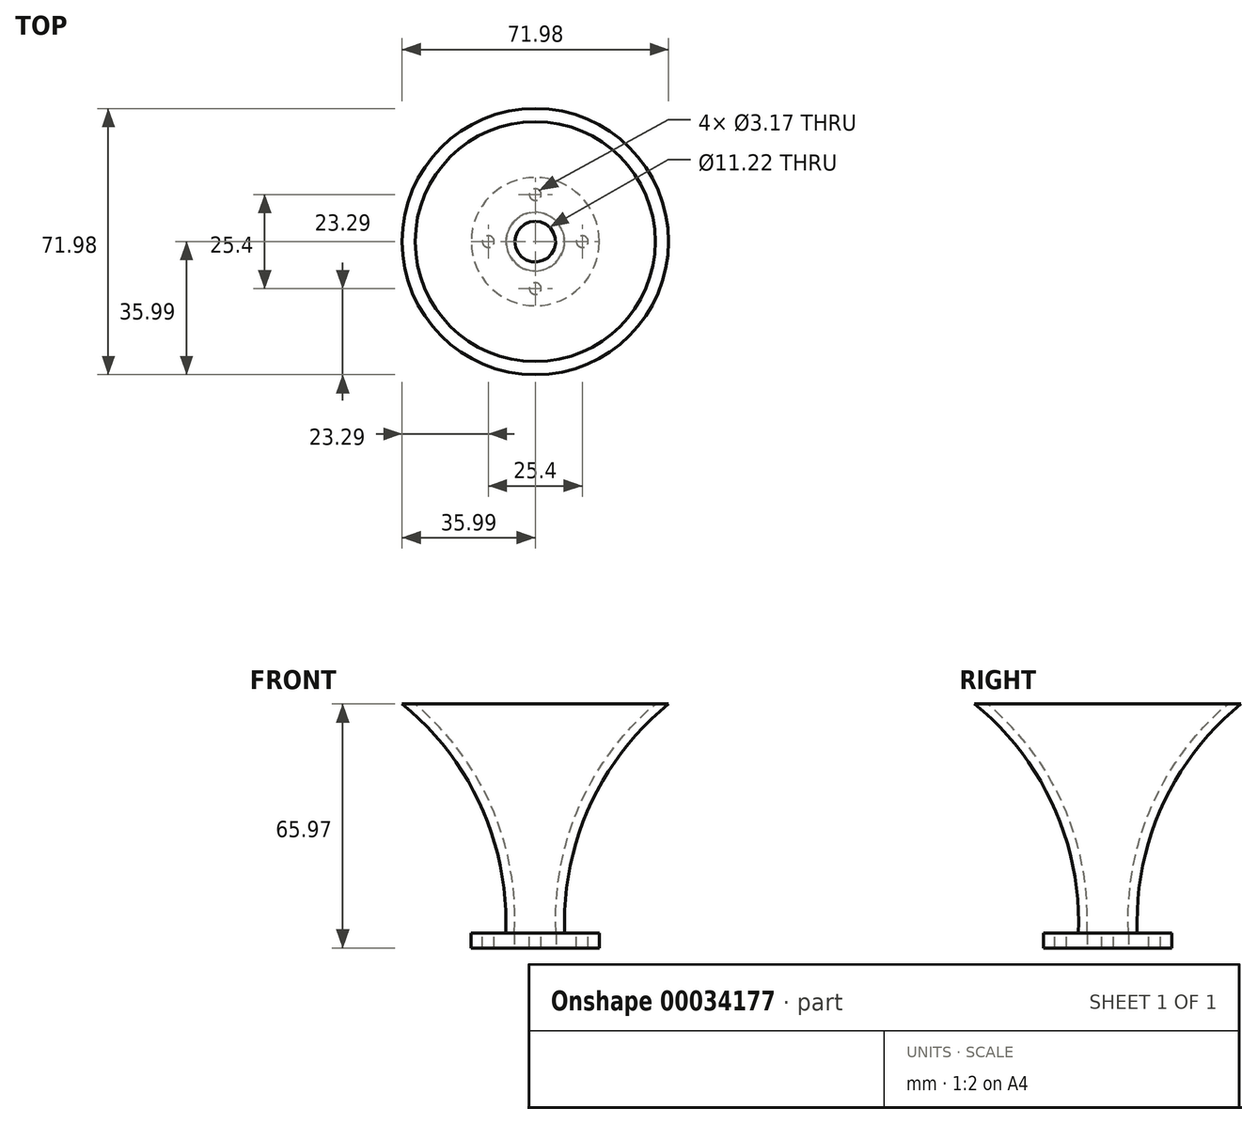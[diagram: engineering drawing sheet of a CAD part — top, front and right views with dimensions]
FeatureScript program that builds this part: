
annotation { "Feature Type Name" : "Feature", "Feature Type Description" : "" }
export const myFeature = defineFeature(function(context is Context, id is Id, definition is map)
    precondition{}
    {
        {
            var Q0;
            Q0=qCreatedBy(makeId("Front.planeOp"),FACE);
            var sketch = newSketch(context, id + "F0", { "sketchPlane" : qUnion([Q0])});
            skLineSegment(sketch, "E0", {"start": v(0, 0) * mm, "end": v(0, 61.95) * mm});
            skArc(sketch, "E1", {"start": v(35.99, 61.95) * mm, "mid": v(14.67, 34.28) * mm, "end": v(7.96, 0) * mm});
            skLineSegment(sketch, "E2", {"start": v(0, 76.37) * mm, "end": v(0, -15.4) * mm, "construction": true});
            skPoint(sketch, "E2.endSnap0", {"position": v(0, 30.98) * mm});
            skArc(sketch, "E3", {"start": v(32.43, 61.9) * mm, "mid": v(11.78, 34.08) * mm, "end": v(5.6, 0) * mm});
            skLineSegment(sketch, "E4", {"start": v(32.43, 61.9) * mm, "end": v(35.99, 61.95) * mm});
            skLineSegment(sketch, "E5", {"start": v(5.6, 0) * mm, "end": v(7.96, 0) * mm});
            skLineSegment(sketch, "E6.bottom", {"start": v(5.6, 0) * mm, "end": v(17.3, 0) * mm});
            skLineSegment(sketch, "E6.top", {"start": v(5.6, -4.02) * mm, "end": v(17.3, -4.02) * mm});
            skLineSegment(sketch, "E6.left", {"start": v(5.6, 0) * mm, "end": v(5.6, -4.02) * mm});
            skLineSegment(sketch, "E6.right", {"start": v(17.3, 0) * mm, "end": v(17.3, -4.02) * mm});
            skSolve(sketch);
        }
        {
            var Q0;
            Q0 = qSketchRegion(id + "F0", true);
            var Q1;
            Q1=sQuery(id+"F0.wireOp",EDGE,"E0");
            revolve(context, id + "F1", {"entities" : qUnion([Q0]), "axis" : qUnion([Q1]), "revolveType" : RevolveType.FULL});
        }
        {
            var Q0;
            Q0=qCreatedBy(makeId("Top.planeOp"),FACE);
            var sketch = newSketch(context, id + "F2", { "sketchPlane" : qUnion([Q0])});
            skCircle(sketch, "E7", {"center": v(0, 0) * mm, "radius": 12.7 * mm, "construction": true});
            skCircle(sketch, "E8", {"center": v(0, -12.7) * mm, "radius": 1.59 * mm});
            skCircle(sketch, "E9.1.0", {"center": v(12.7, 0) * mm, "radius": 1.59 * mm});
            skCircle(sketch, "E9.2.0", {"center": v(0, 12.7) * mm, "radius": 1.59 * mm});
            skCircle(sketch, "E9.3.0", {"center": v(-12.7, 0) * mm, "radius": 1.59 * mm});
            skSolve(sketch);
        }
        {
            var Q0;
            Q0=sQuery(id+"F2.wireOp",VERTEX,"E9.3.0.center");
            var Q1;
            Q1=sQuery(id+"F2.wireOp",VERTEX,"E8.center");
            var Q2;
            Q2=sQuery(id+"F2.wireOp",VERTEX,"E9.1.0.center");
            var Q3;
            Q3=sQuery(id+"F2.wireOp",VERTEX,"E9.2.0.center");
            var Q4;
            Q4=makeQuery(id+"F1.opRevolve","SWEPT_BODY",BODY,{"disambiguationData":[OSD([sQuery(id+"F0.wireOp",EDGE,"E1"),sQuery(id+"F0.wireOp",EDGE,"E3"),sQuery(id+"F0.wireOp",EDGE,"E4"),sQuery(id+"F0.wireOp",EDGE,"E6.bottom"),sQuery(id+"F0.wireOp",EDGE,"E6.top"),sQuery(id+"F0.wireOp",EDGE,"E6.left"),sQuery(id+"F0.wireOp",EDGE,"E6.right")])]});
            hole(context, id + "F3", {"style" : HoleStyle.SIMPLE, "holeDiameter" : 3.17 * mm, "endStyle" : HoleEndStyle.THROUGH, "locations" : qUnion([Q0, Q1, Q2, Q3]), "scope" : qUnion([Q4])});
        }
    });
